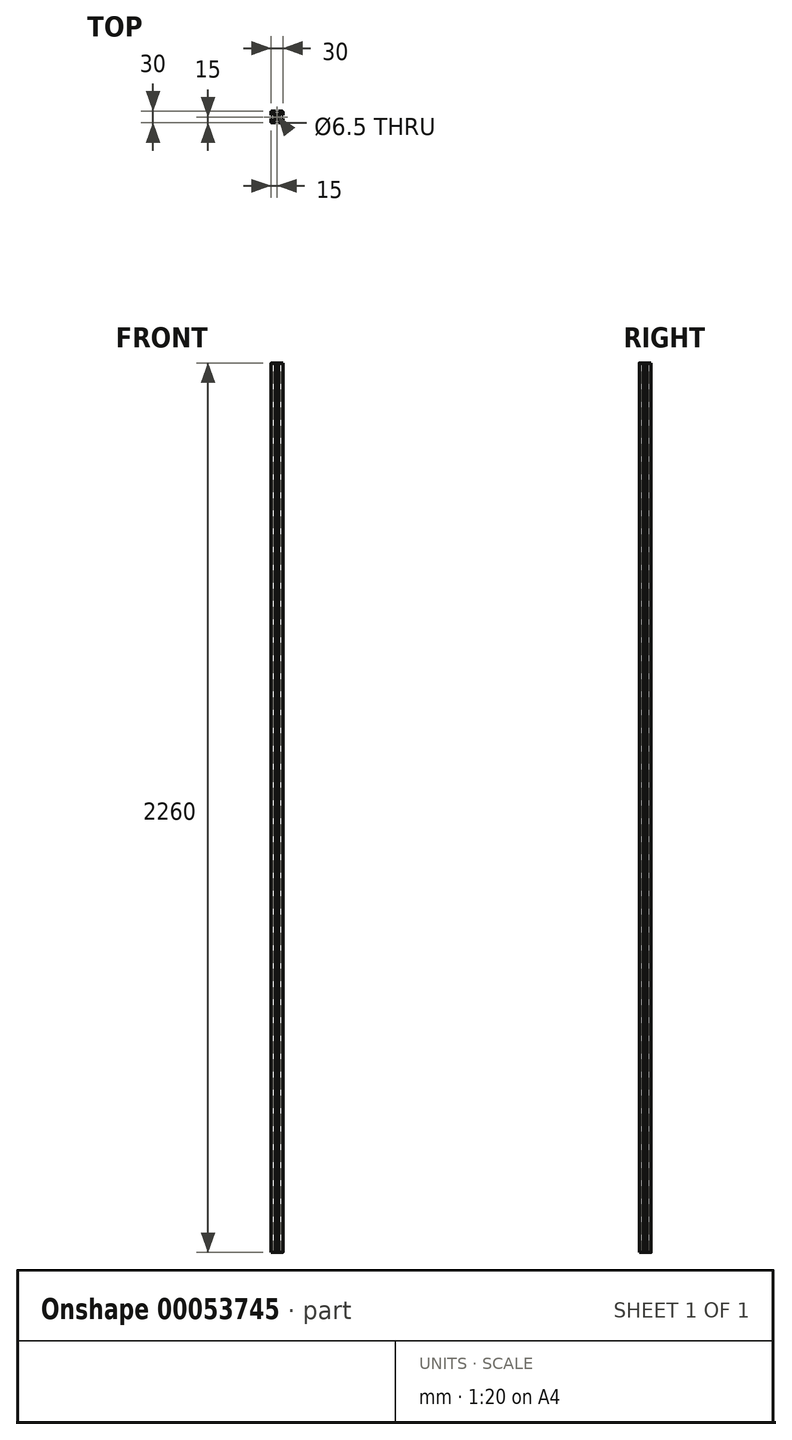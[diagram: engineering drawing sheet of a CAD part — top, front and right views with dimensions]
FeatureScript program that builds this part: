
annotation { "Feature Type Name" : "Feature", "Feature Type Description" : "" }
export const myFeature = defineFeature(function(context is Context, id is Id, definition is map)
    precondition{}
    {
        {
            var Q0;
            Q0=qCreatedBy(makeId("Top.planeOp"),FACE);
            var sketch = newSketch(context, id + "F0", { "sketchPlane" : qUnion([Q0])});
            skLineSegment(sketch, "E0.bottom", {"start": v(-15, 15) * mm, "end": v(15, 15) * mm});
            skLineSegment(sketch, "E0.top", {"start": v(-15, -15) * mm, "end": v(15, -15) * mm});
            skLineSegment(sketch, "E0.left", {"start": v(-15, 15) * mm, "end": v(-15, -15) * mm});
            skLineSegment(sketch, "E0.right", {"start": v(15, 15) * mm, "end": v(15, -15) * mm});
            skSolve(sketch);
        }
        {
            var Q0;
            Q0=qSketchRegion(id+"F0",true);
            extrude(context, id + "F1", {"entities" : qUnion([Q0]), "endBound" : BoundingType.SYMMETRIC, "depth" : 2260 * mm});
        }
        {
            var Q0;
            Q0=makeQuery(id+"F1.opExtrude","SWEPT_EDGE",EDGE,{"disambiguationData":[OSD([sQuery(id+"F0.wireOp",EDGE,"E0.bottom"),sQuery(id+"F0.wireOp",EDGE,"E0.right")])]});
            var Q1;
            Q1=makeQuery(id+"F1.opExtrude","SWEPT_EDGE",EDGE,{"disambiguationData":[OSD([sQuery(id+"F0.wireOp",EDGE,"E0.bottom"),sQuery(id+"F0.wireOp",EDGE,"E0.left")])]});
            var Q2;
            Q2=makeQuery(id+"F1.opExtrude","SWEPT_EDGE",EDGE,{"disambiguationData":[OSD([sQuery(id+"F0.wireOp",EDGE,"E0.top"),sQuery(id+"F0.wireOp",EDGE,"E0.right")])]});
            var Q3;
            Q3=makeQuery(id+"F1.opExtrude","SWEPT_EDGE",EDGE,{"disambiguationData":[OSD([sQuery(id+"F0.wireOp",EDGE,"E0.top"),sQuery(id+"F0.wireOp",EDGE,"E0.left")])]});
            fillet(context, id + "F2", {"entities" : qUnion([Q0, Q1, Q2, Q3]), "radius" : 2 * mm, "tangentPropagation" : true, "allowEdgeOverflow" : false});
        }
        {
            var Q0;
            Q0=makeQuery(id+"F1.opExtrude","CAP_FACE",FACE,{"disambiguationData":[OSD([sQuery(id+"F0.wireOp",EDGE,"E0.bottom"),sQuery(id+"F0.wireOp",EDGE,"E0.top"),sQuery(id+"F0.wireOp",EDGE,"E0.left"),sQuery(id+"F0.wireOp",EDGE,"E0.right")])],"isStart":false});
            var sketch = newSketch(context, id + "F3", { "sketchPlane" : qUnion([Q0])});
            skCircle(sketch, "E1", {"center": v(0, 0) * mm, "radius": 3.25 * mm});
            skSolve(sketch);
        }
        {
            var Q0;
            Q0=qSketchRegion(id+"F3",true);
            extrude(context, id + "F4", {"entities" : qUnion([Q0]), "operationType" : NewBodyOperationType.REMOVE, "endBound" : BoundingType.THROUGH_ALL, "oppositeDirection" : true, "depth" : 25 * mm});
        }
        {
            var Q0;
            Q0=makeQuery(id+"F1.opExtrude","CAP_FACE",FACE,{"disambiguationData":[OSD([sQuery(id+"F0.wireOp",EDGE,"E0.bottom"),sQuery(id+"F0.wireOp",EDGE,"E0.top"),sQuery(id+"F0.wireOp",EDGE,"E0.left"),sQuery(id+"F0.wireOp",EDGE,"E0.right")])],"isStart":false});
            var sketch = newSketch(context, id + "F5", { "sketchPlane" : qUnion([Q0])});
            skLineSegment(sketch, "E2", {"start": v(-4.2, 15) * mm, "end": v(4.2, 15) * mm});
            skLineSegment(sketch, "E3", {"start": v(4.2, 15) * mm, "end": v(4.2, 13) * mm});
            skLineSegment(sketch, "E4", {"start": v(4.2, 13) * mm, "end": v(8.25, 13) * mm});
            skLineSegment(sketch, "E5", {"start": v(8.25, 13) * mm, "end": v(8.25, 10) * mm});
            skLineSegment(sketch, "E6", {"start": v(8.25, 10) * mm, "end": v(3.85, 5.6) * mm});
            skLineSegment(sketch, "E7", {"start": v(3.85, 5.6) * mm, "end": v(-3.85, 5.6) * mm});
            skLineSegment(sketch, "E8", {"start": v(-3.85, 5.6) * mm, "end": v(-8.25, 10) * mm});
            skLineSegment(sketch, "E9", {"start": v(-4.2, 15) * mm, "end": v(-4.2, 13) * mm});
            skLineSegment(sketch, "E10", {"start": v(-4.2, 13) * mm, "end": v(-8.25, 13) * mm});
            skLineSegment(sketch, "E11", {"start": v(-8.25, 13) * mm, "end": v(-8.25, 10) * mm});
            skLineSegment(sketch, "E12.1.0", {"start": v(-15, -4.2) * mm, "end": v(-15, 4.2) * mm});
            skLineSegment(sketch, "E12.1.1", {"start": v(-15, 4.2) * mm, "end": v(-13, 4.2) * mm});
            skLineSegment(sketch, "E12.1.2", {"start": v(-13, 4.2) * mm, "end": v(-13, 8.25) * mm});
            skLineSegment(sketch, "E12.1.3", {"start": v(-13, 8.25) * mm, "end": v(-10, 8.25) * mm});
            skLineSegment(sketch, "E12.1.4", {"start": v(-10, 8.25) * mm, "end": v(-5.6, 3.85) * mm});
            skLineSegment(sketch, "E12.1.5", {"start": v(-5.6, 3.85) * mm, "end": v(-5.6, -3.85) * mm});
            skLineSegment(sketch, "E12.1.6", {"start": v(-5.6, -3.85) * mm, "end": v(-10, -8.25) * mm});
            skLineSegment(sketch, "E12.1.7", {"start": v(-13, -8.25) * mm, "end": v(-10, -8.25) * mm});
            skLineSegment(sketch, "E12.1.8", {"start": v(-13, -4.2) * mm, "end": v(-13, -8.25) * mm});
            skLineSegment(sketch, "E12.1.9", {"start": v(-15, -4.2) * mm, "end": v(-13, -4.2) * mm});
            skLineSegment(sketch, "E12.2.0", {"start": v(4.2, -15) * mm, "end": v(-4.2, -15) * mm});
            skLineSegment(sketch, "E12.2.1", {"start": v(-4.2, -15) * mm, "end": v(-4.2, -13) * mm});
            skLineSegment(sketch, "E12.2.2", {"start": v(-4.2, -13) * mm, "end": v(-8.25, -13) * mm});
            skLineSegment(sketch, "E12.2.3", {"start": v(-8.25, -13) * mm, "end": v(-8.25, -10) * mm});
            skLineSegment(sketch, "E12.2.4", {"start": v(-8.25, -10) * mm, "end": v(-3.85, -5.6) * mm});
            skLineSegment(sketch, "E12.2.5", {"start": v(-3.85, -5.6) * mm, "end": v(3.85, -5.6) * mm});
            skLineSegment(sketch, "E12.2.6", {"start": v(3.85, -5.6) * mm, "end": v(8.25, -10) * mm});
            skLineSegment(sketch, "E12.2.7", {"start": v(8.25, -13) * mm, "end": v(8.25, -10) * mm});
            skLineSegment(sketch, "E12.2.8", {"start": v(4.2, -13) * mm, "end": v(8.25, -13) * mm});
            skLineSegment(sketch, "E12.2.9", {"start": v(4.2, -15) * mm, "end": v(4.2, -13) * mm});
            skLineSegment(sketch, "E12.3.0", {"start": v(15, 4.2) * mm, "end": v(15, -4.2) * mm});
            skLineSegment(sketch, "E12.3.1", {"start": v(15, -4.2) * mm, "end": v(13, -4.2) * mm});
            skLineSegment(sketch, "E12.3.2", {"start": v(13, -4.2) * mm, "end": v(13, -8.25) * mm});
            skLineSegment(sketch, "E12.3.3", {"start": v(13, -8.25) * mm, "end": v(10, -8.25) * mm});
            skLineSegment(sketch, "E12.3.4", {"start": v(10, -8.25) * mm, "end": v(5.6, -3.85) * mm});
            skLineSegment(sketch, "E12.3.5", {"start": v(5.6, -3.85) * mm, "end": v(5.6, 3.85) * mm});
            skLineSegment(sketch, "E12.3.6", {"start": v(5.6, 3.85) * mm, "end": v(10, 8.25) * mm});
            skLineSegment(sketch, "E12.3.7", {"start": v(13, 8.25) * mm, "end": v(10, 8.25) * mm});
            skLineSegment(sketch, "E12.3.8", {"start": v(13, 4.2) * mm, "end": v(13, 8.25) * mm});
            skLineSegment(sketch, "E12.3.9", {"start": v(15, 4.2) * mm, "end": v(13, 4.2) * mm});
            skPoint(sketch, "E12.center", {"position": v(0, 0) * mm});
            skSolve(sketch);
        }
        {
            var Q0;
            Q0=qSketchRegion(id+"F5",true);
            extrude(context, id + "F6", {"entities" : qUnion([Q0]), "operationType" : NewBodyOperationType.REMOVE, "endBound" : BoundingType.THROUGH_ALL, "oppositeDirection" : true, "depth" : 25 * mm});
        }
        {
            var Q0;
            Q0=makeQuery(id+"F1.opExtrude","CAP_FACE",FACE,{"disambiguationData":[OSD([sQuery(id+"F0.wireOp",EDGE,"E0.bottom"),sQuery(id+"F0.wireOp",EDGE,"E0.top"),sQuery(id+"F0.wireOp",EDGE,"E0.left"),sQuery(id+"F0.wireOp",EDGE,"E0.right")])],"isStart":false});
            var sketch = newSketch(context, id + "F7", { "sketchPlane" : qUnion([Q0])});
            skLineSegment(sketch, "E13", {"start": v(15, 4.2) * mm, "end": v(15, -4.2) * mm});
            skLineSegment(sketch, "E14", {"start": v(4.2, 15) * mm, "end": v(-4.2, 15) * mm});
            skLineSegment(sketch, "E15", {"start": v(-15, 4.2) * mm, "end": v(-15, -4.2) * mm});
            skLineSegment(sketch, "E16", {"start": v(4.2, -15) * mm, "end": v(-4.2, -15) * mm});
            skSolve(sketch);
        }
        {
            var Q0;
            Q0=makeQuery(id+"F1.opExtrude","CAP_FACE",FACE,{"disambiguationData":[OSD([sQuery(id+"F0.wireOp",EDGE,"E0.bottom"),sQuery(id+"F0.wireOp",EDGE,"E0.top"),sQuery(id+"F0.wireOp",EDGE,"E0.left"),sQuery(id+"F0.wireOp",EDGE,"E0.right")])],"isStart":true});
            var sketch = newSketch(context, id + "F8", { "sketchPlane" : qUnion([Q0])});
            skLineSegment(sketch, "E17", {"start": v(15, 4.2) * mm, "end": v(15, -4.2) * mm});
            skLineSegment(sketch, "E18", {"start": v(-15, -4.2) * mm, "end": v(-15, 4.2) * mm});
            skLineSegment(sketch, "E19", {"start": v(4.2, 15) * mm, "end": v(-4.2, 15) * mm});
            skLineSegment(sketch, "E20", {"start": v(4.2, -15) * mm, "end": v(-4.2, -15) * mm});
            skSolve(sketch);
        }
    });
